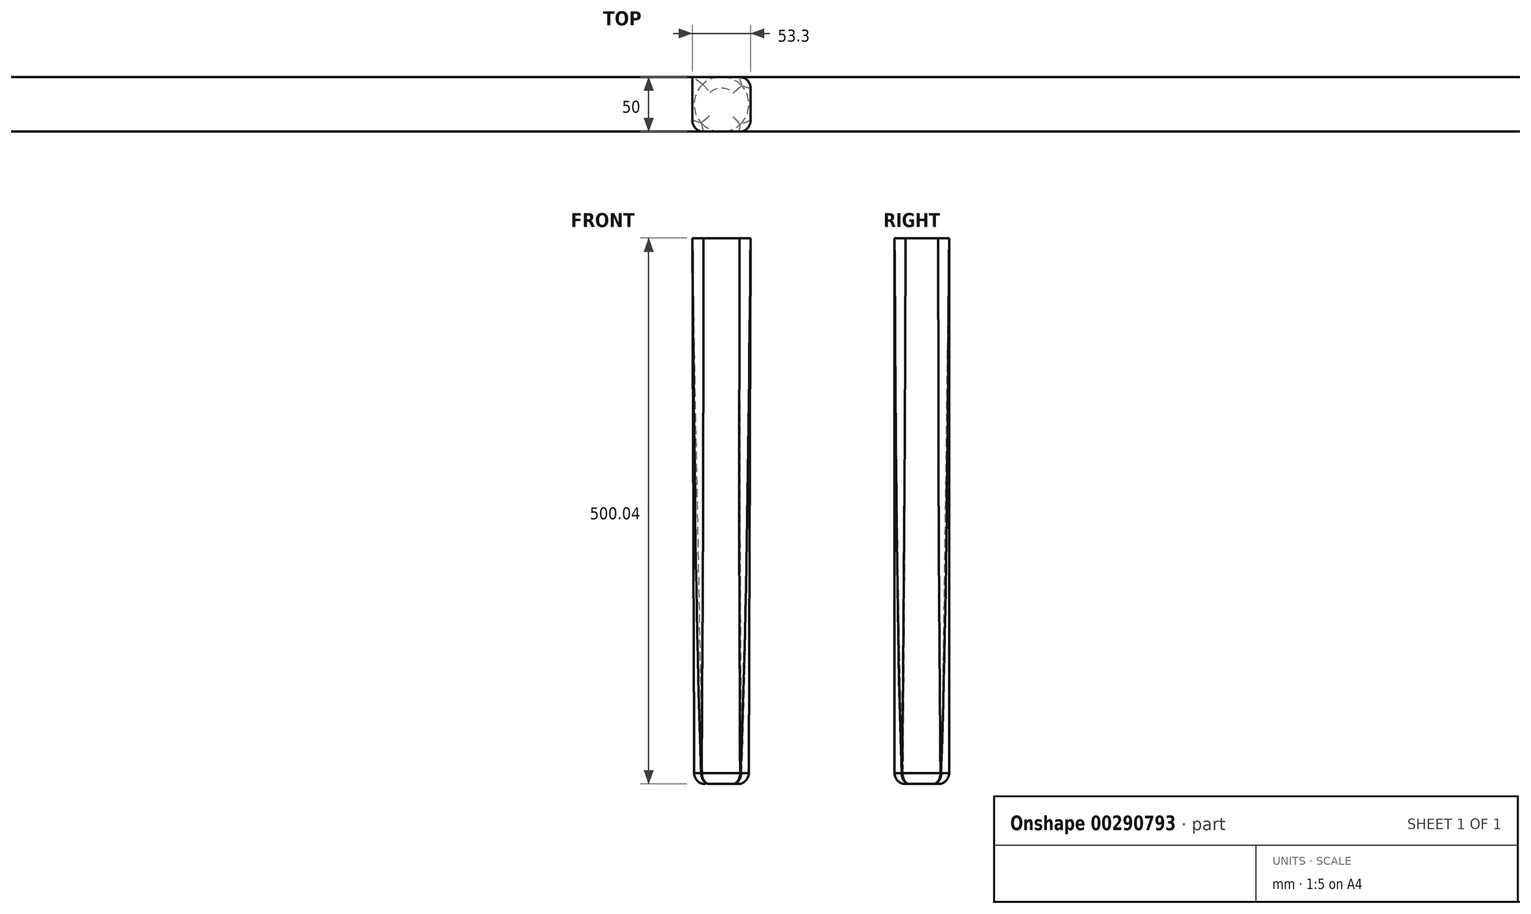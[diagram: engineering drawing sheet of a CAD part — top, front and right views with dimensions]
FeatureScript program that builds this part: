
annotation { "Feature Type Name" : "Feature", "Feature Type Description" : "" }
export const myFeature = defineFeature(function(context is Context, id is Id, definition is map)
    precondition{}
    {
        {
            var Q0;
            Q0=qCreatedBy(makeId("Top.planeOp"),FACE);
            var sketch = newSketch(context, id + "F0", { "sketchPlane" : qUnion([Q0])});
            skCircle(sketch, "E0", {"center": v(0, 0) * mm, "radius": 25 * mm});
            skSolve(sketch);
        }
        {
            var Q0;
            Q0=qCreatedBy(makeId("Top.planeOp"),FACE);
            cPlane(context, id + "F1", {"entities" : qUnion([Q0]), "cplaneType" : CPlaneType.OFFSET, "offset" : 500 * mm, "width" : 150 * mm, "height" : 150 * mm});
        }
        {
            var Q0;
            Q0=qCreatedBy(id+"F1.planeOp",FACE);
            var sketch = newSketch(context, id + "F2", { "sketchPlane" : qUnion([Q0])});
            skLineSegment(sketch, "E1.bottom", {"start": v(26.65, 25) * mm, "end": v(-26.65, 25) * mm});
            skLineSegment(sketch, "E1.top", {"start": v(26.65, -25) * mm, "end": v(-26.65, -25) * mm});
            skLineSegment(sketch, "E1.left", {"start": v(26.65, 25) * mm, "end": v(26.65, -25) * mm});
            skLineSegment(sketch, "E1.right", {"start": v(-26.65, 25) * mm, "end": v(-26.65, -25) * mm});
            skPoint(sketch, "E1.middle", {"position": v(0, 0) * mm});
            skSolve(sketch);
        }
        {
            var Q0;
            Q0=makeQuery(id+"F0.imprint","IMPRINT",FACE,{"disambiguationData":[TD([[makeQuery(id+"F0.imprint","IMPRINT",EDGE,{"derivedFrom":sQuery(id+"F0.wireOp",EDGE,"E0")}),1.0]])]});
            var Q1;
            Q1=makeQuery(id+"F2.imprint","IMPRINT",FACE,{"disambiguationData":[TD([[makeQuery(id+"F2.imprint","IMPRINT",EDGE,{"derivedFrom":sQuery(id+"F2.wireOp",EDGE,"E1.bottom")}),1.0]])]});
            loft(context, id + "F3", {"sheetProfilesArray" : [{ "sheetProfileEntities" : qUnion([Q0]) }, { "sheetProfileEntities" : qUnion([Q1]) }]});
        }
        {
            var Q0;
            Q0=makeQuery(id+"F3.opLoft","SWEPT_EDGE",EDGE,{"disambiguationData":[OSD([sQuery(id+"F0.wireOp",EDGE,"E0"),sQuery(id+"F2.wireOp",EDGE,"E1.top"),sQuery(id+"F2.wireOp",EDGE,"E1.left"),sQuery(id+"F2.wireOp",EDGE,"E1.right")])]});
            var Q1;
            Q1=makeQuery(id+"F3.opLoft","SWEPT_EDGE",EDGE,{"disambiguationData":[OSD([sQuery(id+"F0.wireOp",EDGE,"E0"),sQuery(id+"F2.wireOp",EDGE,"E1.bottom"),sQuery(id+"F2.wireOp",EDGE,"E1.top"),sQuery(id+"F2.wireOp",EDGE,"E1.right")])]});
            var Q2;
            Q2=makeQuery(id+"F3.opLoft","SWEPT_EDGE",EDGE,{"disambiguationData":[OSD([sQuery(id+"F2.wireOp",EDGE,"E1.bottom"),sQuery(id+"F2.wireOp",EDGE,"E1.left")])]});
            var Q3;
            Q3=makeQuery(id+"F3.opLoft","SWEPT_EDGE",EDGE,{"disambiguationData":[OSD([sQuery(id+"F0.wireOp",EDGE,"E0"),sQuery(id+"F2.wireOp",EDGE,"E1.bottom"),sQuery(id+"F2.wireOp",EDGE,"E1.left"),sQuery(id+"F2.wireOp",EDGE,"E1.right")])]});
            var Q4;
            Q4=makeQuery(id+"F3.opLoft","MID_CAP_EDGE",EDGE,{"disambiguationData":[OSD([sQuery(id+"F0.wireOp",EDGE,"E0"),sQuery(id+"F2.wireOp",EDGE,"E1.bottom"),sQuery(id+"F2.wireOp",EDGE,"E1.top"),sQuery(id+"F2.wireOp",EDGE,"E1.left"),sQuery(id+"F2.wireOp",EDGE,"E1.right")])],"capPos":0.0});
            var Q5;
            Q5=makeQuery(id+"F3.opLoft","MID_CAP_EDGE",EDGE,{"disambiguationData":[OSD([sQuery(id+"F0.wireOp",EDGE,"E0"),sQuery(id+"F2.wireOp",EDGE,"E1.bottom"),sQuery(id+"F2.wireOp",EDGE,"E1.top"),sQuery(id+"F2.wireOp",EDGE,"E1.right")])],"capPos":0.0});
            var Q6;
            Q6=makeQuery(id+"F3.opLoft","MID_CAP_EDGE",EDGE,{"disambiguationData":[OSD([sQuery(id+"F0.wireOp",EDGE,"E0"),sQuery(id+"F2.wireOp",EDGE,"E1.bottom"),sQuery(id+"F2.wireOp",EDGE,"E1.left"),sQuery(id+"F2.wireOp",EDGE,"E1.right")])],"capPos":0.0});
            var Q7;
            Q7=makeQuery(id+"F3.opLoft","MID_CAP_EDGE",EDGE,{"disambiguationData":[OSD([sQuery(id+"F0.wireOp",EDGE,"E0"),sQuery(id+"F2.wireOp",EDGE,"E1.bottom"),sQuery(id+"F2.wireOp",EDGE,"E1.left")])],"capPos":0.0});
            fillet(context, id + "F4", {"entities" : qUnion([Q0, Q1, Q2, Q3, Q4, Q5, Q6, Q7]), "radius" : 10 * mm, "tangentPropagation" : true, "allowEdgeOverflow" : false});
        }
    });
